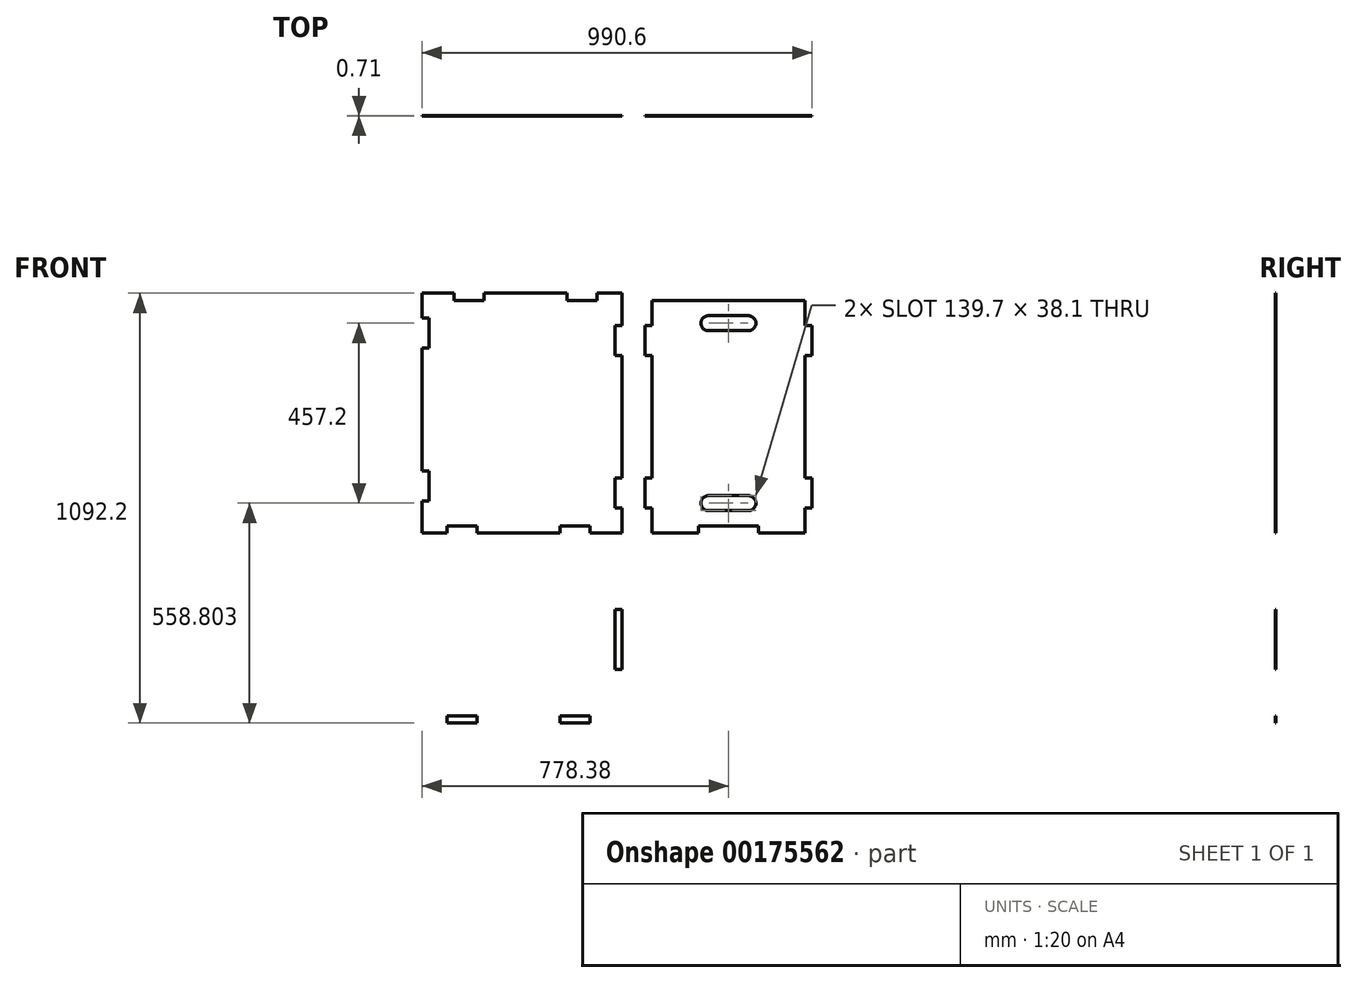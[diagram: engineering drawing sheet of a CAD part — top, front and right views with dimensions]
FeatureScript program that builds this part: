
annotation { "Feature Type Name" : "Feature", "Feature Type Description" : "" }
export const myFeature = defineFeature(function(context is Context, id is Id, definition is map)
    precondition{}
    {
        {
            assignVariable(context, id + "F0", {"name" : "ply34", "anyValue" : .71});
        }
        {
            var Q0;
            Q0=qCreatedBy(makeId("Front.planeOp"),FACE);
            var sketch = newSketch(context, id + "F1", { "sketchPlane" : qUnion([Q0])});
            skLineSegment(sketch, "E0.bottom", {"start": v(-244.98, 194.18) * mm, "end": v(244.98, 194.18) * mm});
            skLineSegment(sketch, "E0.top", {"start": v(-244.98, -194.18) * mm, "end": v(244.98, -194.18) * mm});
            skLineSegment(sketch, "E0.left", {"start": v(-244.98, 194.18) * mm, "end": v(-244.98, -194.18) * mm});
            skLineSegment(sketch, "E0.right", {"start": v(244.98, 194.18) * mm, "end": v(244.98, -194.18) * mm});
            skPoint(sketch, "E0.middle", {"position": v(0, 0) * mm});
            skLineSegment(sketch, "E1.bottom", {"start": v(244.98, 76.2) * mm, "end": v(263.02, 76.2) * mm});
            skLineSegment(sketch, "E1.top", {"start": v(244.98, -76.2) * mm, "end": v(263.02, -76.2) * mm});
            skLineSegment(sketch, "E1.left", {"start": v(244.98, 76.2) * mm, "end": v(244.98, -76.2) * mm});
            skLineSegment(sketch, "E1.right", {"start": v(263.02, 76.2) * mm, "end": v(263.02, -76.2) * mm});
            skPoint(sketch, "E2.oppositeSnap0", {"position": v(254, -76.2) * mm});
            skLineSegment(sketch, "E2.bottom", {"start": v(-244.98, 76.2) * mm, "end": v(-226.95, 76.2) * mm});
            skLineSegment(sketch, "E2.top", {"start": v(-244.98, -76.2) * mm, "end": v(-226.95, -76.2) * mm});
            skLineSegment(sketch, "E2.left", {"start": v(-244.98, 76.2) * mm, "end": v(-244.98, -76.2) * mm});
            skLineSegment(sketch, "E2.right", {"start": v(-226.95, 76.2) * mm, "end": v(-226.95, -76.2) * mm});
            skLineSegment(sketch, "E3", {"start": v(-54.48, 0) * mm, "end": v(72.52, 0) * mm, "construction": true});
            skArc(sketch, "E4.0.startCap", {"start": v(-54.48, -19.05) * mm, "mid": v(-73.53, 0) * mm, "end": v(-54.48, 19.05) * mm, "construction": true});
            skArc(sketch, "E4.0.endCap", {"start": v(72.52, 19.05) * mm, "mid": v(91.57, 0) * mm, "end": v(72.52, -19.05) * mm, "construction": true});
            skLineSegment(sketch, "E4.0.left", {"start": v(-54.48, 19.05) * mm, "end": v(72.52, 19.05) * mm, "construction": true});
            skLineSegment(sketch, "E4.0.right", {"start": v(-54.48, -19.05) * mm, "end": v(72.52, -19.05) * mm, "construction": true});
            skLineSegment(sketch, "E5.bottom", {"start": v(-181.48, 194.18) * mm, "end": v(-105.28, 194.18) * mm});
            skLineSegment(sketch, "E5.top", {"start": v(-181.48, 212.22) * mm, "end": v(-105.28, 212.22) * mm});
            skLineSegment(sketch, "E5.left", {"start": v(-181.48, 194.18) * mm, "end": v(-181.48, 212.22) * mm});
            skLineSegment(sketch, "E5.right", {"start": v(-105.28, 194.18) * mm, "end": v(-105.28, 212.22) * mm});
            skLineSegment(sketch, "E6.bottom", {"start": v(105.28, 194.18) * mm, "end": v(181.48, 194.18) * mm});
            skLineSegment(sketch, "E6.top", {"start": v(105.28, 212.22) * mm, "end": v(181.48, 212.22) * mm});
            skLineSegment(sketch, "E6.left", {"start": v(105.28, 194.18) * mm, "end": v(105.28, 212.22) * mm});
            skLineSegment(sketch, "E6.right", {"start": v(181.48, 194.18) * mm, "end": v(181.48, 212.22) * mm});
            skLineSegment(sketch, "E7.bottom", {"start": v(-244.98, 270.38) * mm, "end": v(263.02, 270.38) * mm});
            skLineSegment(sketch, "E7.top", {"start": v(-244.98, 879.98) * mm, "end": v(263.02, 879.98) * mm});
            skLineSegment(sketch, "E7.left", {"start": v(-244.98, 270.38) * mm, "end": v(-244.98, 879.98) * mm});
            skLineSegment(sketch, "E7.right", {"start": v(263.02, 270.38) * mm, "end": v(263.02, 879.98) * mm});
            skLineSegment(sketch, "E8.bottom", {"start": v(-181.48, 270.38) * mm, "end": v(-105.28, 270.38) * mm});
            skLineSegment(sketch, "E8.top", {"start": v(-181.48, 288.42) * mm, "end": v(-105.28, 288.42) * mm});
            skLineSegment(sketch, "E8.left", {"start": v(-181.48, 270.38) * mm, "end": v(-181.48, 288.42) * mm});
            skLineSegment(sketch, "E8.right", {"start": v(-105.28, 270.38) * mm, "end": v(-105.28, 288.42) * mm});
            skLineSegment(sketch, "E9.bottom", {"start": v(105.28, 270.38) * mm, "end": v(181.48, 270.38) * mm});
            skLineSegment(sketch, "E9.top", {"start": v(105.28, 288.42) * mm, "end": v(181.48, 288.42) * mm});
            skLineSegment(sketch, "E9.left", {"start": v(105.28, 270.38) * mm, "end": v(105.28, 288.42) * mm});
            skLineSegment(sketch, "E9.right", {"start": v(181.48, 270.38) * mm, "end": v(181.48, 288.42) * mm});
            skLineSegment(sketch, "E10.bottom", {"start": v(263.02, 333.88) * mm, "end": v(244.98, 333.88) * mm});
            skLineSegment(sketch, "E10.top", {"start": v(263.02, 410.08) * mm, "end": v(244.98, 410.08) * mm});
            skLineSegment(sketch, "E10.left", {"start": v(263.02, 333.88) * mm, "end": v(263.02, 410.08) * mm});
            skLineSegment(sketch, "E10.right", {"start": v(244.98, 333.88) * mm, "end": v(244.98, 410.08) * mm});
            skLineSegment(sketch, "E11.bottom", {"start": v(263.02, 798.45) * mm, "end": v(244.98, 798.45) * mm});
            skLineSegment(sketch, "E11.top", {"start": v(263.02, 722.25) * mm, "end": v(244.98, 722.25) * mm});
            skLineSegment(sketch, "E11.left", {"start": v(263.02, 798.45) * mm, "end": v(263.02, 722.25) * mm});
            skLineSegment(sketch, "E11.right", {"start": v(244.98, 798.45) * mm, "end": v(244.98, 722.25) * mm});
            skLineSegment(sketch, "E12.bottom", {"start": v(199.52, 879.98) * mm, "end": v(123.32, 879.98) * mm});
            skLineSegment(sketch, "E12.top", {"start": v(199.52, 861.95) * mm, "end": v(123.32, 861.95) * mm});
            skLineSegment(sketch, "E12.left", {"start": v(199.52, 879.98) * mm, "end": v(199.52, 861.95) * mm});
            skLineSegment(sketch, "E12.right", {"start": v(123.32, 879.98) * mm, "end": v(123.32, 861.95) * mm});
            skLineSegment(sketch, "E13.bottom", {"start": v(-163.45, 879.98) * mm, "end": v(-87.25, 879.98) * mm});
            skLineSegment(sketch, "E13.top", {"start": v(-163.45, 861.95) * mm, "end": v(-87.25, 861.95) * mm});
            skLineSegment(sketch, "E13.left", {"start": v(-163.45, 879.98) * mm, "end": v(-163.45, 861.95) * mm});
            skLineSegment(sketch, "E13.right", {"start": v(-87.25, 879.98) * mm, "end": v(-87.25, 861.95) * mm});
            skLineSegment(sketch, "E14.bottom", {"start": v(-244.98, 351.92) * mm, "end": v(-226.95, 351.92) * mm});
            skLineSegment(sketch, "E14.top", {"start": v(-244.98, 428.12) * mm, "end": v(-226.95, 428.12) * mm});
            skLineSegment(sketch, "E14.left", {"start": v(-244.98, 351.92) * mm, "end": v(-244.98, 428.12) * mm});
            skLineSegment(sketch, "E14.right", {"start": v(-226.95, 351.92) * mm, "end": v(-226.95, 428.12) * mm});
            skLineSegment(sketch, "E15.bottom", {"start": v(-244.98, 816.48) * mm, "end": v(-226.95, 816.48) * mm});
            skLineSegment(sketch, "E15.top", {"start": v(-244.98, 740.28) * mm, "end": v(-226.95, 740.28) * mm});
            skLineSegment(sketch, "E15.left", {"start": v(-244.98, 816.48) * mm, "end": v(-244.98, 740.28) * mm});
            skLineSegment(sketch, "E15.right", {"start": v(-226.95, 816.48) * mm, "end": v(-226.95, 740.28) * mm});
            skLineSegment(sketch, "E16", {"start": v(9.02, 76.2) * mm, "end": v(9.02, 0) * mm, "construction": true});
            skLineSegment(sketch, "E17", {"start": v(-226.95, 76.2) * mm, "end": v(244.98, 76.2) * mm, "construction": true});
            skLineSegment(sketch, "E18", {"start": v(263.02, 270.38) * mm, "end": v(727.58, -194.18) * mm, "construction": true});
            skLineSegment(sketch, "E19.bottom", {"start": v(339.22, 270.38) * mm, "end": v(727.58, 270.38) * mm});
            skLineSegment(sketch, "E19.top", {"start": v(339.22, 861.95) * mm, "end": v(727.58, 861.95) * mm});
            skLineSegment(sketch, "E19.left", {"start": v(339.22, 270.38) * mm, "end": v(339.22, 861.95) * mm});
            skLineSegment(sketch, "E19.right", {"start": v(727.58, 270.38) * mm, "end": v(727.58, 861.95) * mm});
            skLineSegment(sketch, "E20", {"start": v(339.22, 333.88) * mm, "end": v(321.18, 333.88) * mm});
            skLineSegment(sketch, "E21", {"start": v(321.18, 333.88) * mm, "end": v(321.18, 410.08) * mm});
            skLineSegment(sketch, "E22", {"start": v(321.18, 410.08) * mm, "end": v(339.22, 410.08) * mm});
            skLineSegment(sketch, "E23", {"start": v(339.22, 722.25) * mm, "end": v(321.18, 722.25) * mm});
            skLineSegment(sketch, "E24", {"start": v(321.18, 722.25) * mm, "end": v(321.18, 798.45) * mm});
            skLineSegment(sketch, "E25", {"start": v(321.18, 798.45) * mm, "end": v(339.22, 798.45) * mm});
            skLineSegment(sketch, "E26.bottom", {"start": v(457.2, 270.38) * mm, "end": v(609.6, 270.38) * mm});
            skLineSegment(sketch, "E26.top", {"start": v(457.2, 288.42) * mm, "end": v(609.6, 288.42) * mm});
            skLineSegment(sketch, "E26.left", {"start": v(457.2, 270.38) * mm, "end": v(457.2, 288.42) * mm});
            skLineSegment(sketch, "E26.right", {"start": v(609.6, 270.38) * mm, "end": v(609.6, 288.42) * mm});
            skLineSegment(sketch, "E27.bottom", {"start": v(457.2, 861.95) * mm, "end": v(609.6, 861.95) * mm});
            skLineSegment(sketch, "E27.top", {"start": v(457.2, 879.98) * mm, "end": v(609.6, 879.98) * mm});
            skLineSegment(sketch, "E27.left", {"start": v(457.2, 861.95) * mm, "end": v(457.2, 879.98) * mm});
            skLineSegment(sketch, "E27.right", {"start": v(609.6, 861.95) * mm, "end": v(609.6, 879.98) * mm});
            skPoint(sketch, "E28", {"position": v(533.4, 270.38) * mm});
            skPoint(sketch, "E29", {"position": v(244.98, 0) * mm});
            skLineSegment(sketch, "E30.MirrorCS", {"start": v(-105.28, -194.18) * mm, "end": v(-105.28, -212.22) * mm});
            skLineSegment(sketch, "E31.MirrorCS", {"start": v(105.28, -194.18) * mm, "end": v(105.28, -212.22) * mm});
            skLineSegment(sketch, "E32.MirrorCS", {"start": v(-181.48, -194.18) * mm, "end": v(-181.48, -212.22) * mm});
            skLineSegment(sketch, "E33.MirrorCS", {"start": v(181.48, -194.18) * mm, "end": v(181.48, -212.22) * mm});
            skLineSegment(sketch, "E34.MirrorCS", {"start": v(105.28, -212.22) * mm, "end": v(181.48, -212.22) * mm});
            skLineSegment(sketch, "E35.MirrorCS", {"start": v(-181.48, -194.18) * mm, "end": v(-105.28, -194.18) * mm});
            skLineSegment(sketch, "E36.MirrorCS", {"start": v(105.28, -194.18) * mm, "end": v(181.48, -194.18) * mm});
            skLineSegment(sketch, "E37.MirrorCS", {"start": v(-181.48, -212.22) * mm, "end": v(-105.28, -212.22) * mm});
            skLineSegment(sketch, "E38", {"start": v(533.4, 288.42) * mm, "end": v(533.4, 861.95) * mm, "construction": true});
            skLineSegment(sketch, "E39.MirrorCS", {"start": v(727.58, 722.25) * mm, "end": v(745.62, 722.25) * mm});
            skLineSegment(sketch, "E40.MirrorCS", {"start": v(727.58, 333.88) * mm, "end": v(745.62, 333.88) * mm});
            skLineSegment(sketch, "E41.MirrorCS", {"start": v(745.62, 798.45) * mm, "end": v(727.58, 798.45) * mm});
            skLineSegment(sketch, "E42.MirrorCS", {"start": v(745.62, 410.08) * mm, "end": v(727.58, 410.08) * mm});
            skLineSegment(sketch, "E43.MirrorCS", {"start": v(745.62, 722.25) * mm, "end": v(745.62, 798.45) * mm});
            skLineSegment(sketch, "E44.MirrorCS", {"start": v(745.62, 333.88) * mm, "end": v(745.62, 410.08) * mm});
            skLineSegment(sketch, "E45", {"start": v(533.4, 346.58) * mm, "end": v(482.6, 346.58) * mm, "construction": true});
            skLineSegment(sketch, "E46", {"start": v(533.4, 346.58) * mm, "end": v(584.2, 346.58) * mm, "construction": true});
            skArc(sketch, "E47.0.startCap", {"start": v(533.4, 327.53) * mm, "mid": v(514.35, 346.58) * mm, "end": v(533.4, 365.63) * mm, "construction": true});
            skArc(sketch, "E47.0.endCap", {"start": v(584.2, 365.63) * mm, "mid": v(603.25, 346.58) * mm, "end": v(584.2, 327.53) * mm});
            skLineSegment(sketch, "E47.0.left", {"start": v(533.4, 365.63) * mm, "end": v(584.2, 365.63) * mm});
            skLineSegment(sketch, "E47.0.right", {"start": v(533.4, 327.53) * mm, "end": v(584.2, 327.53) * mm});
            skArc(sketch, "E47.1.startCap", {"start": v(533.4, 365.63) * mm, "mid": v(552.45, 346.58) * mm, "end": v(533.4, 327.53) * mm, "construction": true});
            skArc(sketch, "E47.1.endCap", {"start": v(482.6, 327.53) * mm, "mid": v(463.55, 346.58) * mm, "end": v(482.6, 365.63) * mm});
            skLineSegment(sketch, "E47.1.left", {"start": v(533.4, 327.53) * mm, "end": v(482.6, 327.53) * mm});
            skLineSegment(sketch, "E47.1.right", {"start": v(533.4, 365.63) * mm, "end": v(482.6, 365.63) * mm});
            skLineSegment(sketch, "E48", {"start": v(263.02, 575.18) * mm, "end": v(-244.98, 575.18) * mm, "construction": true});
            skLineSegment(sketch, "E49.MirrorCS", {"start": v(533.4, 822.83) * mm, "end": v(584.2, 822.83) * mm});
            skArc(sketch, "E50.MirrorCS", {"start": v(533.4, 822.83) * mm, "mid": v(514.35, 803.78) * mm, "end": v(533.4, 784.73) * mm, "construction": true});
            skArc(sketch, "E51.MirrorCS", {"start": v(482.6, 822.83) * mm, "mid": v(463.55, 803.78) * mm, "end": v(482.6, 784.73) * mm});
            skLineSegment(sketch, "E52.MirrorCS", {"start": v(533.4, 784.73) * mm, "end": v(482.6, 784.73) * mm});
            skArc(sketch, "E53.MirrorCS", {"start": v(584.2, 784.73) * mm, "mid": v(603.25, 803.78) * mm, "end": v(584.2, 822.83) * mm});
            skLineSegment(sketch, "E54.MirrorCS", {"start": v(533.4, 822.83) * mm, "end": v(482.6, 822.83) * mm});
            skArc(sketch, "E55.MirrorCS", {"start": v(533.4, 784.73) * mm, "mid": v(552.45, 803.78) * mm, "end": v(533.4, 822.83) * mm, "construction": true});
            skLineSegment(sketch, "E56.MirrorCS", {"start": v(533.4, 803.78) * mm, "end": v(482.6, 803.78) * mm, "construction": true});
            skLineSegment(sketch, "E57.MirrorCS", {"start": v(533.4, 803.78) * mm, "end": v(584.2, 803.78) * mm, "construction": true});
            skLineSegment(sketch, "E58.MirrorCS", {"start": v(533.4, 784.73) * mm, "end": v(584.2, 784.73) * mm});
            skSolve(sketch);
        }
        {
            var Q0;
            Q0=makeQuery(id+"F1.imprint","IMPRINT",FACE,{"disambiguationData":[TD([[makeQuery(id+"F1.imprint","IMPRINT",EDGE,{"derivedFrom":sQuery(id+"F1.wireOp",EDGE,"kCc1j6ts-heYF-Fn3p-T1Or-9dhK8fWiCS55.bottom")}),1.0]])]});
            var Q1;
            {var subQ14=sQuery(id+"F1.wireOp",EDGE,"VwTwZ1sW-8fcc-gWBe-9lOO-Ow4Tpcl8XJWt.left");Q1=makeQuery(id+"F1.imprint","IMPRINT",FACE,{"disambiguationData":[TD([[makeQuery(id+"F1.imprint","IMPRINT",EDGE,{"derivedFrom":subQ14}),1.0]])]});}
            var Q2;
            Q2=makeQuery(id+"F1.imprint","IMPRINT",FACE,{"disambiguationData":[TD([[makeQuery(id+"F1.imprint","IMPRINT",EDGE,{"derivedFrom":sQuery(id+"F1.wireOp",EDGE,"jVbOSFHp-gFmB-nsM2-l99k-Lf8UrlLDHhPC.bottom")}),-1.0]])]});
            var Q3;
            Q3=makeQuery(id+"F1.imprint","IMPRINT",FACE,{"disambiguationData":[TD([[makeQuery(id+"F1.imprint","IMPRINT",EDGE,{"derivedFrom":sQuery(id+"F1.wireOp",EDGE,"E1.bottom")}),-1.0]])]});
            var Q4;
            Q4=makeQuery(id+"F1.imprint","IMPRINT",FACE,{"disambiguationData":[TD([[makeQuery(id+"F1.imprint","IMPRINT",EDGE,{"derivedFrom":sQuery(id+"F1.wireOp",EDGE,"E5.bottom")}),1.0]])]});
            var Q5;
            Q5=makeQuery(id+"F1.imprint","IMPRINT",FACE,{"disambiguationData":[TD([[makeQuery(id+"F1.imprint","IMPRINT",EDGE,{"derivedFrom":sQuery(id+"F1.wireOp",EDGE,"E6.bottom")}),1.0]])]});
            var Q6;
            Q6=makeQuery(id+"F1.imprint","IMPRINT",FACE,{"disambiguationData":[TD([[makeQuery(id+"F1.imprint","IMPRINT",EDGE,{"derivedFrom":sQuery(id+"F1.wireOp",EDGE,"E8.top")}),1.0]])]});
            var Q7;
            Q7=makeQuery(id+"F1.imprint","IMPRINT",FACE,{"disambiguationData":[TD([[makeQuery(id+"F1.imprint","IMPRINT",EDGE,{"derivedFrom":sQuery(id+"F1.wireOp",EDGE,"E26.top")}),1.0]])]});
            var Q8;
            Q8=makeQuery(id+"F1.imprint","IMPRINT",FACE,{"disambiguationData":[TD([[makeQuery(id+"F1.imprint","IMPRINT",EDGE,{"derivedFrom":sQuery(id+"F1.wireOp",EDGE,"E27.bottom")}),1.0]])]});
            var Q9;
            {var subQ0=sQuery(id+"F1.wireOp",EDGE,"E23");Q9=makeQuery(id+"F1.imprint","IMPRINT",FACE,{"disambiguationData":[TD([[makeQuery(id+"F1.imprint","IMPRINT",EDGE,{"derivedFrom":subQ0}),-1.0]])]});}
            var Q10;
            {var subQ0=sQuery(id+"F1.wireOp",EDGE,"E20");Q10=makeQuery(id+"F1.imprint","IMPRINT",FACE,{"disambiguationData":[TD([[makeQuery(id+"F1.imprint","IMPRINT",EDGE,{"derivedFrom":subQ0}),-1.0]])]});}
            var Q11;
            {var subQ3=sQuery(id+"F1.wireOp",EDGE,"E1.left");Q11=makeQuery(id+"F1.imprint","IMPRINT",FACE,{"disambiguationData":[TD([[makeQuery(id+"F1.imprint","IMPRINT",EDGE,{"derivedFrom":subQ3}),-1.0]])]});}
            var Q12;
            Q12=makeQuery(id+"F1.imprint","IMPRINT",FACE,{"disambiguationData":[TD([[makeQuery(id+"F1.imprint","IMPRINT",EDGE,{"derivedFrom":sQuery(id+"F1.wireOp",EDGE,"E30.MirrorCS")}),-1.0]])]});
            var Q13;
            Q13=makeQuery(id+"F1.imprint","IMPRINT",FACE,{"disambiguationData":[TD([[makeQuery(id+"F1.imprint","IMPRINT",EDGE,{"derivedFrom":sQuery(id+"F1.wireOp",EDGE,"E31.MirrorCS")}),1.0]])]});
            var Q14;
            {var subQ0=sQuery(id+"F1.wireOp",EDGE,"E39.MirrorCS");Q14=makeQuery(id+"F1.imprint","IMPRINT",FACE,{"disambiguationData":[TD([[makeQuery(id+"F1.imprint","IMPRINT",EDGE,{"derivedFrom":subQ0}),1.0]])]});}
            var Q15;
            {var subQ0=sQuery(id+"F1.wireOp",EDGE,"E40.MirrorCS");Q15=makeQuery(id+"F1.imprint","IMPRINT",FACE,{"disambiguationData":[TD([[makeQuery(id+"F1.imprint","IMPRINT",EDGE,{"derivedFrom":subQ0}),1.0]])]});}
            extrude(context, id + "F2", {"entities" : qUnion([Q0, Q1, Q2, Q3, Q4, Q5, Q6, Q7, Q8, Q9, Q10, Q11, Q12, Q13, Q14, Q15]), "offsetDistance" : 25.4 * mm, "depth" : (getVariable(context, 'ply34')) * mm});
        }
    });
